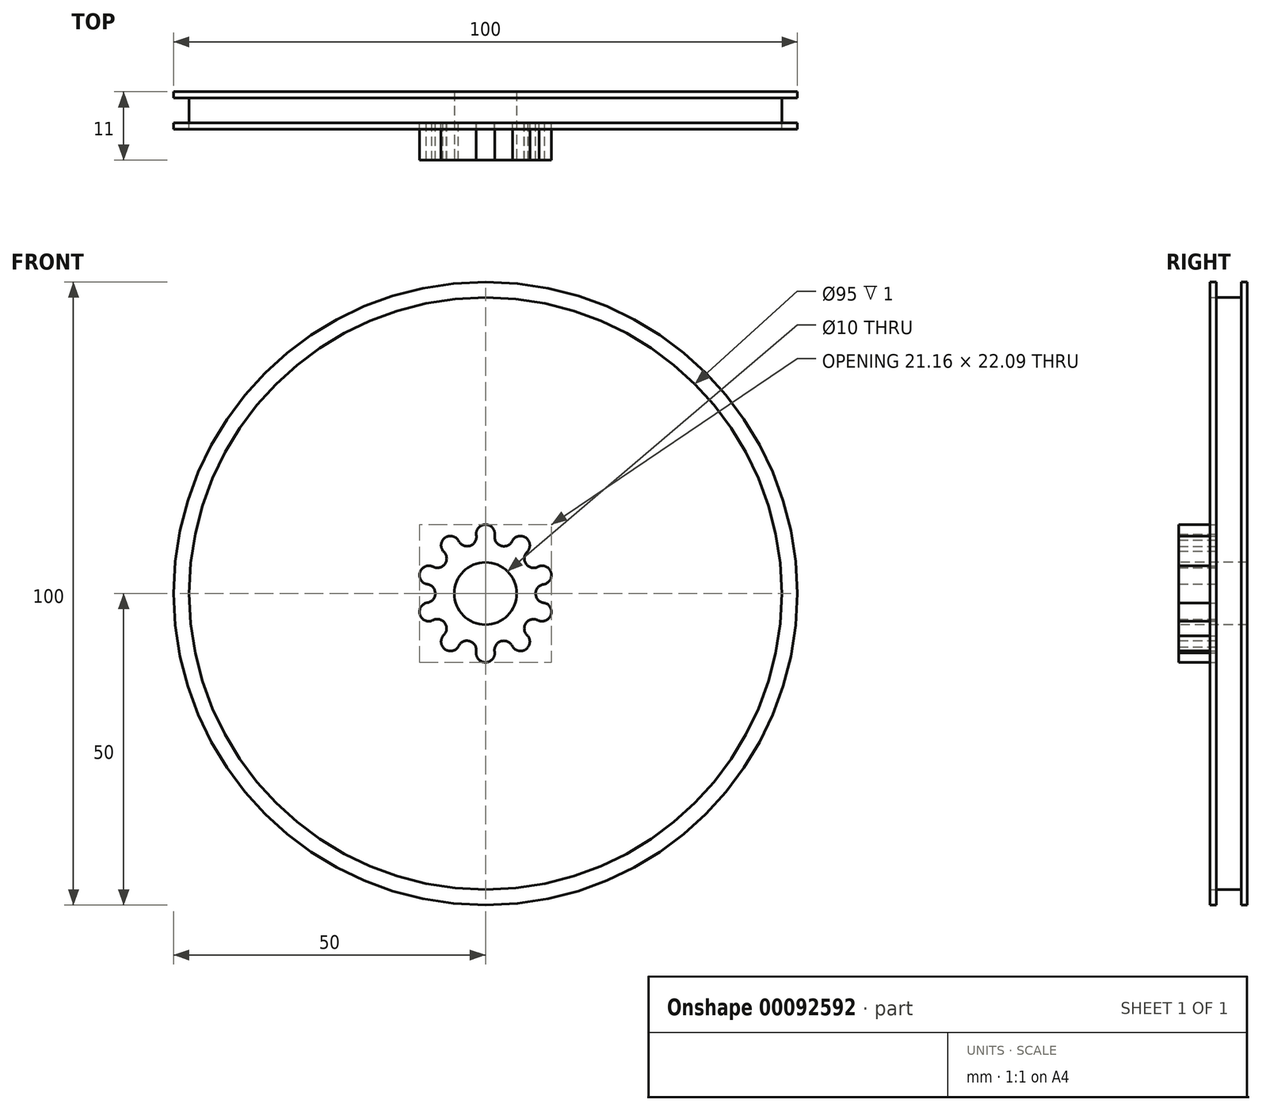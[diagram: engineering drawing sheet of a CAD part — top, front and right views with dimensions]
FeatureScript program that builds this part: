
annotation { "Feature Type Name" : "Feature", "Feature Type Description" : "" }
export const myFeature = defineFeature(function(context is Context, id is Id, definition is map)
    precondition{}
    {
        {
            var Q0;
            Q0=qCreatedBy(makeId("Front.planeOp"),FACE);
            var sketch = newSketch(context, id + "F0", { "sketchPlane" : qUnion([Q0])});
            skCircle(sketch, "E0", {"center": v(0, 0) * mm, "radius": 50 * mm});
            skSolve(sketch);
        }
        {
            var Q0;
            Q0=makeQuery(id+"F0.imprint","IMPRINT",FACE,{"disambiguationData":[TD([[makeQuery(id+"F0.imprint","IMPRINT",EDGE,{"derivedFrom":sQuery(id+"F0.wireOp",EDGE,"E0")}),1.0]])]});
            extrude(context, id + "F1", {"entities" : qUnion([Q0]), "depth" : 1 * mm});
        }
        {
            var Q0;
            Q0=makeQuery(id+"F1.opExtrude","CAP_FACE",FACE,{"disambiguationData":[OSD([sQuery(id+"F0.wireOp",EDGE,"E0")])],"isStart":false});
            var sketch = newSketch(context, id + "F2", { "sketchPlane" : qUnion([Q0])});
            skCircle(sketch, "E1", {"center": v(0, 0) * mm, "radius": 47.5 * mm});
            skSolve(sketch);
        }
        {
            var Q0;
            Q0=makeQuery(id+"F2.imprint","IMPRINT",FACE,{"disambiguationData":[TD([[makeQuery(id+"F2.imprint","IMPRINT",EDGE,{"derivedFrom":sQuery(id+"F2.wireOp",EDGE,"E1")}),1.0]])]});
            extrude(context, id + "F3", {"entities" : qUnion([Q0]), "operationType" : NewBodyOperationType.ADD, "depth" : 4 * mm});
        }
        {
            var Q0;
            Q0=makeQuery(id+"F3.opExtrude","CAP_FACE",FACE,{"disambiguationData":[OSD([sQuery(id+"F2.wireOp",EDGE,"E1")])],"isStart":false});
            var sketch = newSketch(context, id + "F4", { "sketchPlane" : qUnion([Q0])});
            skCircle(sketch, "E2", {"center": v(0, 0) * mm, "radius": 50 * mm});
            skSolve(sketch);
        }
        {
            var Q0;
            Q0=makeQuery(id+"F4.imprint","IMPRINT",FACE,{"disambiguationData":[TD([[makeQuery(id+"F4.imprint","IMPRINT",EDGE,{"derivedFrom":sQuery(id+"F4.wireOp",EDGE,"E2")}),1.0]])]});
            extrude(context, id + "F5", {"entities" : qUnion([Q0]), "depth" : 1 * mm});
        }
        {
            var Q0;
            Q0=makeQuery(id+"F3.opExtrude","CAP_FACE",FACE,{"disambiguationData":[OSD([sQuery(id+"F2.wireOp",EDGE,"E1")])],"isStart":false});
            var sketch = newSketch(context, id + "F6", { "sketchPlane" : qUnion([Q0])});
            skLineSegment(sketch, "E3", {"start": v(0, 0) * mm, "end": v(0, 9.55) * mm});
            skArc(sketch, "E4", {"start": v(1.48, 9.31) * mm, "mid": v(0.06, 11.05) * mm, "end": v(-1.5, 9.43) * mm});
            skArc(sketch, "E5", {"start": v(1.48, 9.31) * mm, "mid": v(2.6, 7.63) * mm, "end": v(4.37, 8.57) * mm});
            skArc(sketch, "E6.1.0", {"start": v(-4.28, 8.4) * mm, "mid": v(-6.45, 8.97) * mm, "end": v(-6.75, 6.75) * mm});
            skArc(sketch, "E6.1.1", {"start": v(-4.28, 8.4) * mm, "mid": v(-2.39, 7.7) * mm, "end": v(-1.5, 9.5) * mm});
            skArc(sketch, "E6.2.0", {"start": v(-8.4, 4.29) * mm, "mid": v(-10.49, 3.47) * mm, "end": v(-9.43, 1.5) * mm});
            skArc(sketch, "E6.2.1", {"start": v(-8.4, 4.29) * mm, "mid": v(-6.45, 4.82) * mm, "end": v(-6.8, 6.8) * mm});
            skArc(sketch, "E6.3.0", {"start": v(-9.32, -1.47) * mm, "mid": v(-10.53, -3.36) * mm, "end": v(-8.5, -4.34) * mm});
            skArc(sketch, "E6.3.1", {"start": v(-9.32, -1.47) * mm, "mid": v(-8.05, 0.1) * mm, "end": v(-9.5, 1.51) * mm});
            skArc(sketch, "E6.4.0", {"start": v(-6.67, -6.66) * mm, "mid": v(-6.54, -8.9) * mm, "end": v(-4.33, -8.5) * mm});
            skArc(sketch, "E6.4.1", {"start": v(-6.67, -6.66) * mm, "mid": v(-6.58, -4.65) * mm, "end": v(-8.58, -4.36) * mm});
            skArc(sketch, "E6.5.0", {"start": v(-1.48, -9.31) * mm, "mid": v(-0.06, -11.05) * mm, "end": v(1.5, -9.43) * mm});
            skArc(sketch, "E6.5.1", {"start": v(-1.48, -9.31) * mm, "mid": v(-2.6, -7.63) * mm, "end": v(-4.37, -8.57) * mm});
            skArc(sketch, "E6.6.0", {"start": v(4.28, -8.4) * mm, "mid": v(6.45, -8.97) * mm, "end": v(6.75, -6.75) * mm});
            skArc(sketch, "E6.6.1", {"start": v(4.28, -8.4) * mm, "mid": v(2.39, -7.7) * mm, "end": v(1.5, -9.5) * mm});
            skArc(sketch, "E6.7.0", {"start": v(8.4, -4.29) * mm, "mid": v(10.49, -3.47) * mm, "end": v(9.43, -1.5) * mm});
            skArc(sketch, "E6.7.1", {"start": v(8.4, -4.29) * mm, "mid": v(6.45, -4.82) * mm, "end": v(6.8, -6.8) * mm});
            skArc(sketch, "E6.8.0", {"start": v(9.32, 1.47) * mm, "mid": v(10.53, 3.36) * mm, "end": v(8.5, 4.34) * mm});
            skArc(sketch, "E6.8.1", {"start": v(9.32, 1.47) * mm, "mid": v(8.05, -0.1) * mm, "end": v(9.5, -1.51) * mm});
            skArc(sketch, "E6.9.0", {"start": v(6.67, 6.66) * mm, "mid": v(6.54, 8.9) * mm, "end": v(4.33, 8.5) * mm});
            skArc(sketch, "E6.9.1", {"start": v(6.67, 6.66) * mm, "mid": v(6.58, 4.65) * mm, "end": v(8.58, 4.36) * mm});
            skPoint(sketch, "E6.center", {"position": v(0, 0) * mm});
            skPoint(sketch, "E7.orphan", {"position": v(-1.48, 9.43) * mm});
            skPoint(sketch, "E8.orphan", {"position": v(4.35, 8.5) * mm});
            skPoint(sketch, "E9.orphan", {"position": v(8.51, 4.32) * mm});
            skPoint(sketch, "E10.orphan", {"position": v(9.43, -1.5) * mm});
            skPoint(sketch, "E11.orphan", {"position": v(6.74, -6.76) * mm});
            skPoint(sketch, "E12.orphan", {"position": v(1.48, -9.43) * mm});
            skPoint(sketch, "E13.orphan", {"position": v(-4.35, -8.5) * mm});
            skPoint(sketch, "E14.orphan", {"position": v(-8.51, -4.32) * mm});
            skPoint(sketch, "E15.orphan", {"position": v(-9.43, 1.5) * mm});
            skPoint(sketch, "E16.orphan", {"position": v(-6.74, 6.76) * mm});
            skSolve(sketch);
        }
        {
            var Q0;
            {var subQ10=sQuery(id+"F6.wireOp",EDGE,"E5");Q0=makeQuery(id+"F6.imprint","IMPRINT",FACE,{"disambiguationData":[TD([[makeQuery(id+"F6.imprint","IMPRINT",EDGE,{"derivedFrom":subQ10}),-1.0]])]});}
            extrude(context, id + "F7", {"entities" : qUnion([Q0]), "operationType" : NewBodyOperationType.ADD, "depth" : 6 * mm});
        }
        {
            var Q0;
            Q0=makeQuery(id+"F3.opExtrude","CAP_FACE",FACE,{"disambiguationData":[OSD([sQuery(id+"F2.wireOp",EDGE,"E1")])],"isStart":false});
            extrude(context, id + "F8", {"entities" : qUnion([Q0]), "depth" : 1 * mm});
        }
        {
            var Q0;
            Q0=makeQuery(id+"F7.opExtrude","CAP_FACE",FACE,{"disambiguationData":[OSD([sQuery(id+"F6.wireOp",EDGE,"E4"),sQuery(id+"F6.wireOp",EDGE,"E5"),sQuery(id+"F6.wireOp",EDGE,"E6.1.0"),sQuery(id+"F6.wireOp",EDGE,"E6.1.1"),sQuery(id+"F6.wireOp",EDGE,"E6.2.0"),sQuery(id+"F6.wireOp",EDGE,"E6.2.1"),sQuery(id+"F6.wireOp",EDGE,"E6.3.0"),sQuery(id+"F6.wireOp",EDGE,"E6.3.1"),sQuery(id+"F6.wireOp",EDGE,"E6.4.0"),sQuery(id+"F6.wireOp",EDGE,"E6.4.1"),sQuery(id+"F6.wireOp",EDGE,"E6.5.0"),sQuery(id+"F6.wireOp",EDGE,"E6.5.1"),sQuery(id+"F6.wireOp",EDGE,"E6.6.0"),sQuery(id+"F6.wireOp",EDGE,"E6.6.1"),sQuery(id+"F6.wireOp",EDGE,"E6.7.0"),sQuery(id+"F6.wireOp",EDGE,"E6.7.1"),sQuery(id+"F6.wireOp",EDGE,"E6.8.0"),sQuery(id+"F6.wireOp",EDGE,"E6.8.1"),sQuery(id+"F6.wireOp",EDGE,"E6.9.0"),sQuery(id+"F6.wireOp",EDGE,"E6.9.1")])],"isStart":false});
            var sketch = newSketch(context, id + "F9", { "sketchPlane" : qUnion([Q0])});
            skCircle(sketch, "E17", {"center": v(0, 0) * mm, "radius": 5 * mm});
            skSolve(sketch);
        }
        {
            var Q0;
            Q0=makeQuery(id+"F9.imprint","IMPRINT",FACE,{"disambiguationData":[TD([[makeQuery(id+"F9.imprint","IMPRINT",EDGE,{"derivedFrom":sQuery(id+"F9.wireOp",EDGE,"E17")}),1.0]])]});
            extrude(context, id + "F10", {"entities" : qUnion([Q0]), "operationType" : NewBodyOperationType.REMOVE, "oppositeDirection" : true, "depth" : 25 * mm});
        }
    });
